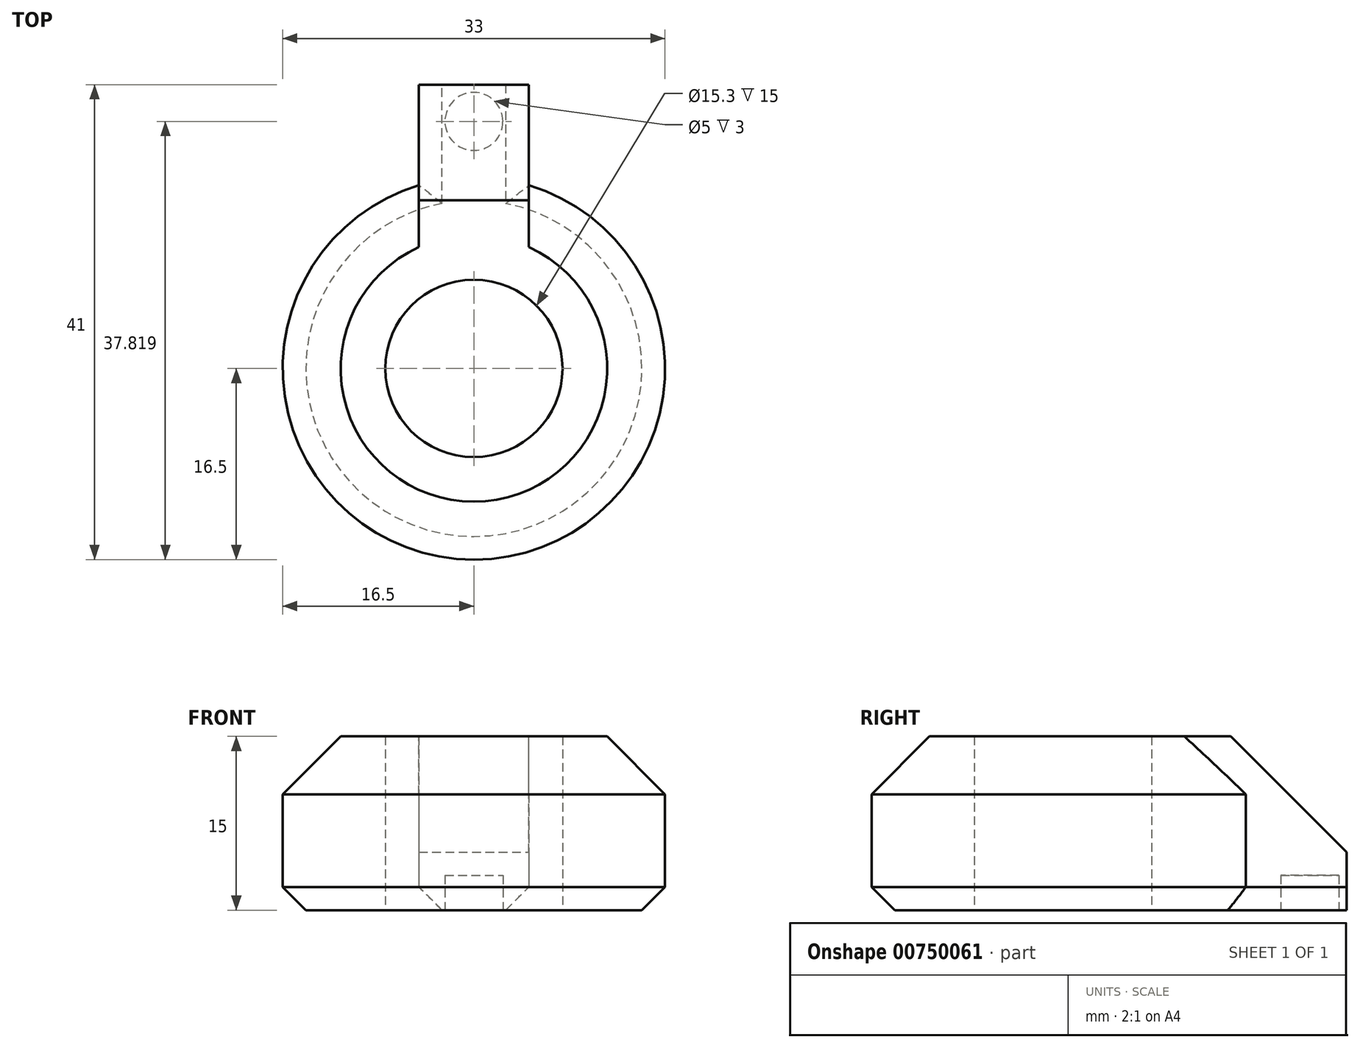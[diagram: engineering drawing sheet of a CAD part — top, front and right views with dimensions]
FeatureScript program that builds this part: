
annotation { "Feature Type Name" : "Feature", "Feature Type Description" : "" }
export const myFeature = defineFeature(function(context is Context, id is Id, definition is map)
    precondition{}
    {
        {
            var Q0;
            Q0=qCreatedBy(makeId("Top.planeOp"),FACE);
            var sketch = newSketch(context, id + "F0", { "sketchPlane" : qUnion([Q0])});
            skCircle(sketch, "E0", {"center": v(0, 0) * mm, "radius": 16.5 * mm});
            skCircle(sketch, "E1", {"center": v(0, 0) * mm, "radius": 7.65 * mm});
            skLineSegment(sketch, "E2.top", {"start": v(4.75, 24.5) * mm, "end": v(-4.75, 24.5) * mm});
            skLineSegment(sketch, "E2.left", {"start": v(4.75, 15.8) * mm, "end": v(4.75, 24.5) * mm});
            skLineSegment(sketch, "E2.right", {"start": v(-4.75, 15.8) * mm, "end": v(-4.75, 24.5) * mm});
            skSolve(sketch);
        }
        {
            var Q0;
            Q0=makeQuery(id+"F0.imprint","IMPRINT",FACE,{"disambiguationData":[TD([[makeQuery(id+"F0.imprint","IMPRINT",EDGE,{"derivedFrom":sQuery(id+"F0.wireOp",EDGE,"E1")}),-1.0]])]});
            var Q1;
            Q1=makeQuery(id+"F0.imprint","IMPRINT",FACE,{"disambiguationData":[TD([[makeQuery(id+"F0.imprint","IMPRINT",EDGE,{"derivedFrom":sQuery(id+"F0.wireOp",EDGE,"E2.top")}),1.0]])]});
            extrude(context, id + "F1", {"entities" : qUnion([Q0, Q1]), "depth" : 15 * mm, "offsetDistance" : 25 * mm});
        }
        {
            var Q0;
            Q0=makeQuery(id+"F1.opExtrude","CAP_EDGE",EDGE,{"disambiguationData":[OSD([sQuery(id+"F0.wireOp",EDGE,"E2.top")])],"isStart":false});
            chamfer(context, id + "F2", {"entities" : qUnion([Q0]), "width" : 10 * mm, "tangentPropagation" : true});
        }
        {
            var Q0;
            Q0=makeQuery(id+"F1.opExtrude","CAP_EDGE",EDGE,{"disambiguationData":[OSD([sQuery(id+"F0.wireOp",EDGE,"E0")])],"isStart":false});
            chamfer(context, id + "F3", {"entities" : qUnion([Q0]), "width" : 5 * mm, "tangentPropagation" : true});
        }
        {
            var Q0;
            Q0=makeQuery(id+"F1.opExtrude","CAP_EDGE",EDGE,{"disambiguationData":[OSD([sQuery(id+"F0.wireOp",EDGE,"E2.right")])],"isStart":true});
            var Q1;
            Q1=makeQuery(id+"F1.opExtrude","CAP_EDGE",EDGE,{"disambiguationData":[OSD([sQuery(id+"F0.wireOp",EDGE,"E2.left")])],"isStart":true});
            var Q2;
            Q2=makeQuery(id+"F1.opExtrude","CAP_EDGE",EDGE,{"disambiguationData":[OSD([sQuery(id+"F0.wireOp",EDGE,"E0")])],"isStart":true});
            chamfer(context, id + "F4", {"entities" : qUnion([Q0, Q1, Q2]), "width" : 2 * mm, "tangentPropagation" : true});
        }
        {
            var Q0;
            Q0=makeQuery(id+"F1.opExtrude","CAP_FACE",FACE,{"disambiguationData":[OSD([sQuery(id+"F0.wireOp",EDGE,"E0"),sQuery(id+"F0.wireOp",EDGE,"E1"),sQuery(id+"F0.wireOp",EDGE,"E2.top"),sQuery(id+"F0.wireOp",EDGE,"E2.left"),sQuery(id+"F0.wireOp",EDGE,"E2.right")])],"isStart":true});
            var sketch = newSketch(context, id + "F5", { "sketchPlane" : qUnion([Q0])});
            skCircle(sketch, "E3", {"center": v(0, -21.32) * mm, "radius": 2.5 * mm});
            skSolve(sketch);
        }
        {
            var Q0;
            Q0=makeQuery(id+"F5.imprint","IMPRINT",FACE,{"disambiguationData":[TD([[makeQuery(id+"F5.imprint","IMPRINT",EDGE,{"derivedFrom":sQuery(id+"F5.wireOp",EDGE,"E3")}),1.0]])]});
            extrude(context, id + "F6", {"entities" : qUnion([Q0]), "operationType" : NewBodyOperationType.REMOVE, "oppositeDirection" : true, "depth" : 3 * mm, "offsetDistance" : 25 * mm});
        }
    });
